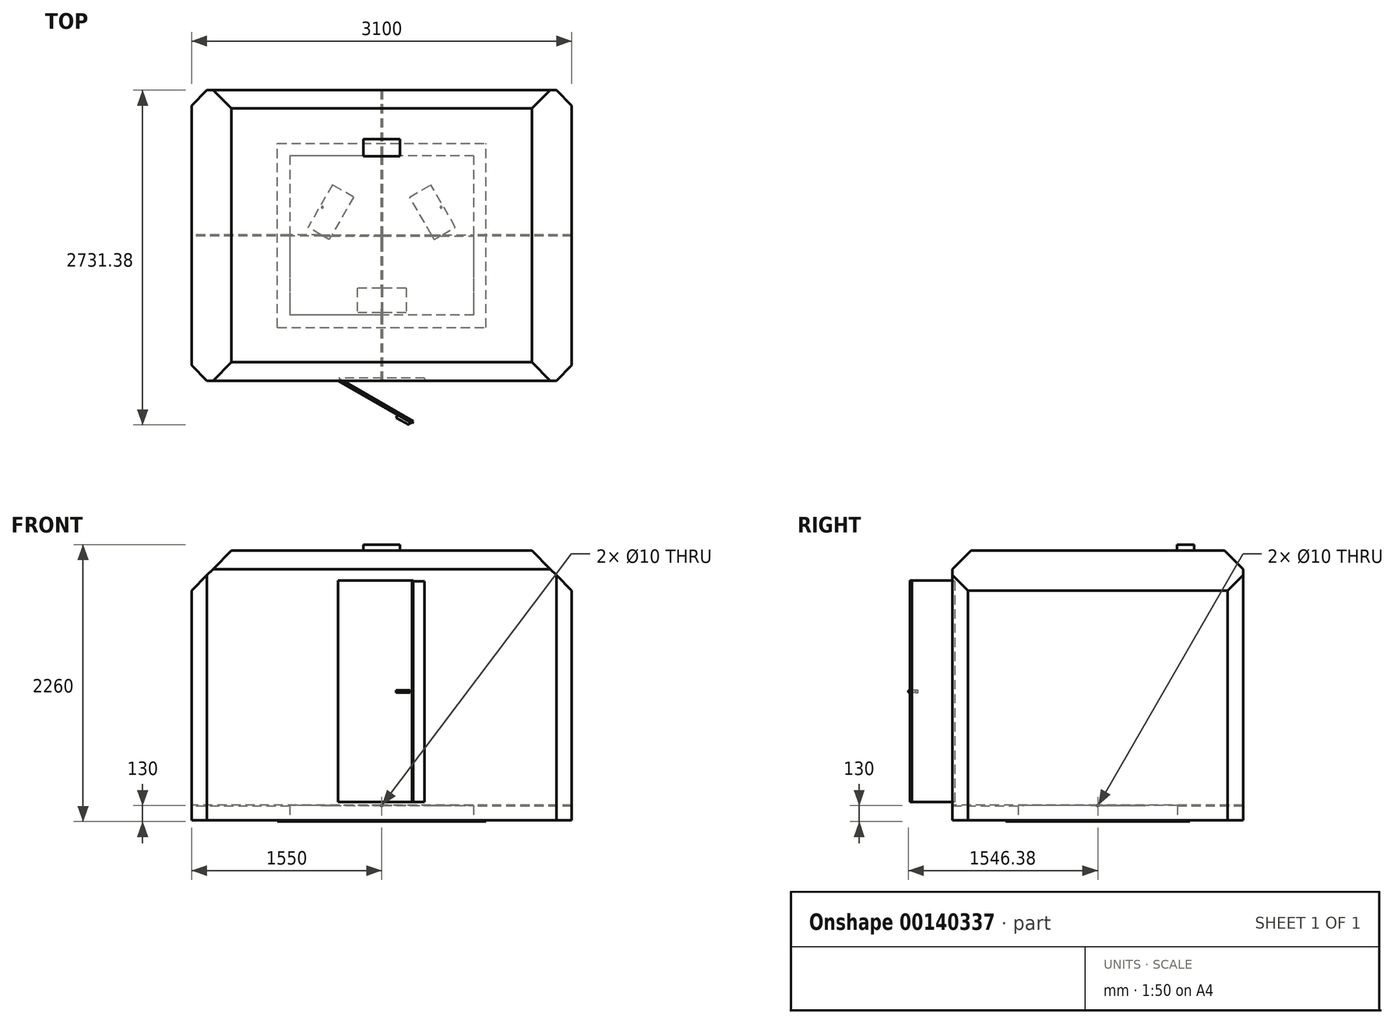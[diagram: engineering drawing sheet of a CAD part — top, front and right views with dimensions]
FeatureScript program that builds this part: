
annotation { "Feature Type Name" : "Feature", "Feature Type Description" : "" }
export const myFeature = defineFeature(function(context is Context, id is Id, definition is map)
    precondition{}
    {
        {
            var Q0;
            Q0=qCreatedBy(makeId("Front.planeOp"),FACE);
            var sketch = newSketch(context, id + "F0", { "sketchPlane" : qUnion([Q0])});
            skLineSegment(sketch, "E0.bottom", {"start": v(1550, -1100) * mm, "end": v(-1550, -1100) * mm});
            skLineSegment(sketch, "E0.top", {"start": v(1550, 1100) * mm, "end": v(-1550, 1100) * mm});
            skLineSegment(sketch, "E0.left", {"start": v(1550, -1100) * mm, "end": v(1550, 1100) * mm});
            skLineSegment(sketch, "E0.right", {"start": v(-1550, -1100) * mm, "end": v(-1550, 1100) * mm});
            skPoint(sketch, "E0.middle", {"position": v(0, 0) * mm});
            skSolve(sketch);
        }
        {
            var Q0;
            Q0 = qSketchRegion(id + "F0", true);
            extrude(context, id + "F1", {"entities" : qUnion([Q0]), "depth" : 2370 * mm});
        }
        {
            var Q0;
            Q0=makeQuery(id+"F1.opExtrude","SWEPT_EDGE",EDGE,{"disambiguationData":[OSD([sQuery(id+"F0.wireOp",EDGE,"E0.top"),sQuery(id+"F0.wireOp",EDGE,"E0.right")])]});
            chamfer(context, id + "F2", {"entities" : qUnion([Q0]), "width" : 325 * mm, "tangentPropagation" : true});
        }
        {
            var Q0;
            Q0=makeQuery(id+"F1.opExtrude","SWEPT_EDGE",EDGE,{"disambiguationData":[OSD([sQuery(id+"F0.wireOp",EDGE,"E0.top"),sQuery(id+"F0.wireOp",EDGE,"E0.left")])]});
            chamfer(context, id + "F3", {"entities" : qUnion([Q0]), "width" : 325 * mm, "tangentPropagation" : true});
        }
        {
            var Q0;
            Q0=makeQuery(id+"F1.opExtrude","CAP_EDGE",EDGE,{"disambiguationData":[OSD([sQuery(id+"F0.wireOp",EDGE,"E0.left")])],"isStart":false});
            chamfer(context, id + "F4", {"entities" : qUnion([Q0]), "width" : 125 * mm, "tangentPropagation" : true});
        }
        {
            var Q0;
            Q0=makeQuery(id+"F1.opExtrude","CAP_EDGE",EDGE,{"disambiguationData":[OSD([sQuery(id+"F0.wireOp",EDGE,"E0.right")])],"isStart":false});
            chamfer(context, id + "F5", {"entities" : qUnion([Q0]), "width" : 125 * mm, "tangentPropagation" : true});
        }
        {
            var Q0;
            Q0=makeQuery(id+"F1.opExtrude","CAP_EDGE",EDGE,{"disambiguationData":[OSD([sQuery(id+"F0.wireOp",EDGE,"E0.right")])],"isStart":true});
            chamfer(context, id + "F6", {"entities" : qUnion([Q0]), "width" : 125 * mm, "tangentPropagation" : true});
        }
        {
            var Q0;
            Q0=makeQuery(id+"F1.opExtrude","CAP_EDGE",EDGE,{"disambiguationData":[OSD([sQuery(id+"F0.wireOp",EDGE,"E0.left")])],"isStart":true});
            chamfer(context, id + "F7", {"entities" : qUnion([Q0]), "width" : 125 * mm, "tangentPropagation" : true});
        }
        {
            var Q0;
            Q0=makeQuery(id+"F1.opExtrude","SWEPT_FACE",FACE,{"disambiguationData":[OSD([sQuery(id+"F0.wireOp",EDGE,"E0.bottom")])]});
            var sketch = newSketch(context, id + "F8", { "sketchPlane" : qUnion([Q0])});
            skLineSegment(sketch, "E1", {"start": v(0, 0) * mm, "end": v(0, 2370) * mm, "construction": true});
            skLineSegment(sketch, "E2", {"start": v(-1550, 1185) * mm, "end": v(1550, 1185) * mm, "construction": true});
            skLineSegment(sketch, "E3.bottom", {"start": v(750, 535) * mm, "end": v(-750, 535) * mm});
            skLineSegment(sketch, "E3.top", {"start": v(750, 1835) * mm, "end": v(-750, 1835) * mm});
            skLineSegment(sketch, "E3.left", {"start": v(750, 535) * mm, "end": v(750, 1835) * mm});
            skLineSegment(sketch, "E3.right", {"start": v(-750, 535) * mm, "end": v(-750, 1835) * mm});
            skPoint(sketch, "E3.middle", {"position": v(0, 1185) * mm});
            skSolve(sketch);
        }
        {
            var Q0;
            Q0 = qSketchRegion(id + "F8", true);
            extrude(context, id + "F9", {"entities" : qUnion([Q0]), "operationType" : NewBodyOperationType.REMOVE, "oppositeDirection" : true, "depth" : 120 * mm});
        }
        {
            var Q0;
            Q0=makeQuery(id+"F9.boolean.opBoolean","COPY",FACE,{"derivedFrom":makeQuery(id+"F9.opExtrude","CAP_FACE",FACE,{"disambiguationData":[OSD([sQuery(id+"F8.wireOp",EDGE,"E3.bottom"),sQuery(id+"F8.wireOp",EDGE,"E3.top"),sQuery(id+"F8.wireOp",EDGE,"E3.left"),sQuery(id+"F8.wireOp",EDGE,"E3.right")])],"isStart":false})});
            var sketch = newSketch(context, id + "F10", { "sketchPlane" : qUnion([Q0])});
            skLineSegment(sketch, "E4", {"start": v(0, 1835) * mm, "end": v(0, 1235) * mm, "construction": true});
            skLineSegment(sketch, "E5.bottom", {"start": v(200, 1614) * mm, "end": v(-200, 1614) * mm});
            skLineSegment(sketch, "E5.top", {"start": v(200, 1814) * mm, "end": v(-200, 1814) * mm});
            skLineSegment(sketch, "E5.left", {"start": v(200, 1614) * mm, "end": v(200, 1814) * mm});
            skLineSegment(sketch, "E5.right", {"start": v(-200, 1614) * mm, "end": v(-200, 1814) * mm});
            skPoint(sketch, "E5.middle", {"position": v(0, 1714) * mm});
            skLineSegment(sketch, "E6", {"start": v(0, 1235) * mm, "end": v(-409.07, 998.82) * mm, "construction": true});
            skLineSegment(sketch, "E7", {"start": v(0, 1235) * mm, "end": v(395.82, 1006.47) * mm, "construction": true});
            skCircle(sketch, "E8", {"center": v(0, 1235) * mm, "radius": 559 * mm, "construction": true});
            skCircle(sketch, "E9", {"center": v(0, 1794) * mm, "radius": 7.5 * mm});
            skCircle(sketch, "E10.MirrorC", {"center": v(484.1, 955.5) * mm, "radius": 7.5 * mm});
            skCircle(sketch, "E11.MirrorC", {"center": v(-484.1, 955.5) * mm, "radius": 7.5 * mm});
            skLineSegment(sketch, "E12", {"start": v(750, 1185) * mm, "end": v(-750, 1185) * mm, "construction": true});
            skLineSegment(sketch, "E13.MirrorCS", {"start": v(428.22, 1218.7) * mm, "end": v(228.22, 872.3) * mm});
            skLineSegment(sketch, "E14.MirrorCS", {"start": v(228.22, 872.3) * mm, "end": v(401.43, 772.3) * mm});
            skLineSegment(sketch, "E15.MirrorCS", {"start": v(601.43, 1118.7) * mm, "end": v(401.43, 772.3) * mm});
            skLineSegment(sketch, "E16.MirrorCS", {"start": v(428.22, 1218.7) * mm, "end": v(601.43, 1118.7) * mm});
            skLineSegment(sketch, "E17.MirrorCS", {"start": v(-428.22, 1218.7) * mm, "end": v(-601.43, 1118.7) * mm});
            skLineSegment(sketch, "E18.MirrorCS", {"start": v(-401.43, 772.3) * mm, "end": v(-601.43, 1118.7) * mm});
            skLineSegment(sketch, "E19.MirrorCS", {"start": v(-228.22, 872.3) * mm, "end": v(-401.43, 772.3) * mm});
            skLineSegment(sketch, "E20.MirrorCS", {"start": v(-228.22, 872.3) * mm, "end": v(-428.22, 1218.7) * mm});
            skCircle(sketch, "E21", {"center": v(0, 1235) * mm, "radius": 7.5 * mm});
            skSolve(sketch);
        }
        {
            var Q0;
            Q0 = qSketchRegion(id + "F10", true);
            extrude(context, id + "F11", {"entities" : qUnion([Q0]), "operationType" : NewBodyOperationType.REMOVE, "oppositeDirection" : true, "depth" : 1 * mm});
        }
        {
            var Q0;
            Q0=makeQuery(id+"F9.boolean.opBoolean","COPY",FACE,{"derivedFrom":makeQuery(id+"F9.opExtrude","SWEPT_FACE",FACE,{"disambiguationData":[OSD([sQuery(id+"F8.wireOp",EDGE,"E3.right")])]})});
            var sketch = newSketch(context, id + "F12", { "sketchPlane" : qUnion([Q0])});
            skCircle(sketch, "E22", {"center": v(-1185, -980) * mm, "radius": 5 * mm});
            skSolve(sketch);
        }
        {
            var Q0;
            Q0 = qSketchRegion(id + "F12", true);
            extrude(context, id + "F13", {"entities" : qUnion([Q0]), "operationType" : NewBodyOperationType.REMOVE, "depth" : 1 * mm});
        }
        {
            var Q0;
            Q0 = qSketchRegion(id + "F12", true);
            extrude(context, id + "F14", {"entities" : qUnion([Q0]), "operationType" : NewBodyOperationType.REMOVE, "endBound" : BoundingType.THROUGH_ALL, "oppositeDirection" : true, "depth" : 25 * mm, "hasSecondDirection" : true, "secondDirectionBound" : SecondDirectionBoundingType.THROUGH_ALL, "secondDirectionOppositeDirection" : false, "secondDirectionDepth" : 25 * mm});
        }
        {
            var Q0;
            Q0=makeQuery(id+"F9.boolean.opBoolean","COPY",FACE,{"derivedFrom":makeQuery(id+"F9.opExtrude","SWEPT_FACE",FACE,{"disambiguationData":[OSD([sQuery(id+"F8.wireOp",EDGE,"E3.bottom")])]})});
            var sketch = newSketch(context, id + "F15", { "sketchPlane" : qUnion([Q0])});
            skLineSegment(sketch, "E23", {"start": v(0, -1100) * mm, "end": v(0, -980) * mm, "construction": true});
            skCircle(sketch, "E24", {"center": v(0, -980) * mm, "radius": 5 * mm});
            skSolve(sketch);
        }
        {
            var Q0;
            Q0 = qSketchRegion(id + "F15", true);
            extrude(context, id + "F16", {"entities" : qUnion([Q0]), "operationType" : NewBodyOperationType.REMOVE, "endBound" : BoundingType.THROUGH_ALL, "oppositeDirection" : true, "depth" : 25 * mm, "hasSecondDirection" : true, "secondDirectionBound" : SecondDirectionBoundingType.THROUGH_ALL, "secondDirectionOppositeDirection" : false, "secondDirectionDepth" : 25 * mm});
        }
        {
            var Q0;
            Q0=makeQuery(id+"F1.opExtrude","CAP_EDGE",EDGE,{"disambiguationData":[OSD([sQuery(id+"F0.wireOp",EDGE,"E0.top")])],"isStart":true});
            chamfer(context, id + "F17", {"entities" : qUnion([Q0]), "width" : 150 * mm, "tangentPropagation" : true});
        }
        {
            var Q0;
            Q0=makeQuery(id+"F1.opExtrude","CAP_EDGE",EDGE,{"disambiguationData":[OSD([sQuery(id+"F0.wireOp",EDGE,"E0.top")])],"isStart":false});
            chamfer(context, id + "F18", {"entities" : qUnion([Q0]), "width" : 150 * mm, "tangentPropagation" : true});
        }
        {
            var Q0;
            Q0=makeQuery(id+"F1.opExtrude","SWEPT_FACE",FACE,{"disambiguationData":[OSD([sQuery(id+"F0.wireOp",EDGE,"E0.bottom")])]});
            var sketch = newSketch(context, id + "F19", { "sketchPlane" : qUnion([Q0])});
            skLineSegment(sketch, "E25.bottom", {"start": v(-850, 1935) * mm, "end": v(850, 1935) * mm});
            skLineSegment(sketch, "E25.top", {"start": v(-850, 435) * mm, "end": v(850, 435) * mm});
            skLineSegment(sketch, "E25.left", {"start": v(-850, 1935) * mm, "end": v(-850, 435) * mm});
            skLineSegment(sketch, "E25.right", {"start": v(850, 1935) * mm, "end": v(850, 435) * mm});
            skLineSegment(sketch, "E26.bottom", {"start": v(-750, 535) * mm, "end": v(750, 535) * mm});
            skLineSegment(sketch, "E26.top", {"start": v(-750, 1835) * mm, "end": v(750, 1835) * mm});
            skLineSegment(sketch, "E26.left", {"start": v(-750, 535) * mm, "end": v(-750, 1835) * mm});
            skLineSegment(sketch, "E26.right", {"start": v(750, 535) * mm, "end": v(750, 1835) * mm});
            skSolve(sketch);
        }
        {
            var Q0;
            Q0 = qSketchRegion(id + "F19", true);
            extrude(context, id + "F20", {"entities" : qUnion([Q0]), "operationType" : NewBodyOperationType.ADD, "depth" : 10 * mm});
        }
        {
            var Q0;
            Q0=makeQuery(id+"F1.opExtrude","CAP_FACE",FACE,{"disambiguationData":[OSD([sQuery(id+"F0.wireOp",EDGE,"E0.bottom"),sQuery(id+"F0.wireOp",EDGE,"E0.top"),sQuery(id+"F0.wireOp",EDGE,"E0.left"),sQuery(id+"F0.wireOp",EDGE,"E0.right")])],"isStart":false});
            var sketch = newSketch(context, id + "F21", { "sketchPlane" : qUnion([Q0])});
            skLineSegment(sketch, "E27", {"start": v(0, 950) * mm, "end": v(0, -367.55) * mm, "construction": true});
            skPoint(sketch, "E28.middle", {"position": v(0, -75) * mm});
            skPoint(sketch, "E29.middle", {"position": v(0, -1025) * mm});
            skLineSegment(sketch, "E30.bottom", {"start": v(350, -950) * mm, "end": v(-350, -950) * mm});
            skLineSegment(sketch, "E30.top", {"start": v(350, 850) * mm, "end": v(-350, 850) * mm});
            skLineSegment(sketch, "E30.left", {"start": v(350, -950) * mm, "end": v(350, 850) * mm});
            skLineSegment(sketch, "E30.right", {"start": v(-350, -950) * mm, "end": v(-350, 850) * mm});
            skPoint(sketch, "E30.middle", {"position": v(0, -50) * mm});
            skSolve(sketch);
        }
        {
            var Q0;
            Q0 = qSketchRegion(id + "F21", true);
            extrude(context, id + "F22", {"entities" : qUnion([Q0]), "operationType" : NewBodyOperationType.REMOVE, "oppositeDirection" : true, "depth" : 20 * mm});
        }
        {
            var Q0;
            Q0=makeQuery(id+"F1.opExtrude","SWEPT_FACE",FACE,{"disambiguationData":[OSD([sQuery(id+"F0.wireOp",EDGE,"E0.top")])]});
            var sketch = newSketch(context, id + "F23", { "sketchPlane" : qUnion([Q0])});
            skLineSegment(sketch, "E31", {"start": v(0, -150) * mm, "end": v(0, -1860.94) * mm, "construction": true});
            skPoint(sketch, "E31.endSnap0", {"position": v(0, -150) * mm});
            skLineSegment(sketch, "E32.bottom", {"start": v(150, -540) * mm, "end": v(-150, -540) * mm});
            skLineSegment(sketch, "E32.top", {"start": v(150, -400) * mm, "end": v(-150, -400) * mm});
            skLineSegment(sketch, "E32.left", {"start": v(150, -540) * mm, "end": v(150, -400) * mm});
            skLineSegment(sketch, "E32.right", {"start": v(-150, -540) * mm, "end": v(-150, -400) * mm});
            skPoint(sketch, "E32.middle", {"position": v(0, -470) * mm});
            skSolve(sketch);
        }
        {
            var Q0;
            Q0 = qSketchRegion(id + "F23", true);
            extrude(context, id + "F24", {"entities" : qUnion([Q0]), "operationType" : NewBodyOperationType.ADD, "depth" : 50 * mm});
        }
        {
            var Q0;
            Q0=makeQuery(id+"F22.boolean.opBoolean","COPY",FACE,{"derivedFrom":makeQuery(id+"F22.opExtrude","SWEPT_FACE",FACE,{"disambiguationData":[OSD([sQuery(id+"F21.wireOp",EDGE,"E30.bottom")])]})});
            var sketch = newSketch(context, id + "F25", { "sketchPlane" : qUnion([Q0])});
            skLineSegment(sketch, "E33.bottom", {"start": v(-360, -2367.32) * mm, "end": v(246.22, -2717.32) * mm});
            skLineSegment(sketch, "E33.top", {"start": v(-350, -2350) * mm, "end": v(256.22, -2700) * mm});
            skLineSegment(sketch, "E33.left", {"start": v(-360, -2367.32) * mm, "end": v(-350, -2350) * mm});
            skLineSegment(sketch, "E33.right", {"start": v(246.22, -2717.32) * mm, "end": v(256.22, -2700) * mm});
            skSolve(sketch);
        }
        {
            var Q0;
            Q0 = qSketchRegion(id + "F25", true);
            extrude(context, id + "F26", {"entities" : qUnion([Q0]), "operationType" : NewBodyOperationType.ADD, "depth" : 1805 * mm});
        }
        {
            var Q0;
            Q0=makeQuery(id+"F26.opExtrude","SWEPT_FACE",FACE,{"disambiguationData":[OSD([sQuery(id+"F25.wireOp",EDGE,"E33.bottom")])]});
            var sketch = newSketch(context, id + "F27", { "sketchPlane" : qUnion([Q0])});
            skLineSegment(sketch, "E34.bottom", {"start": v(1436.7, -57.5) * mm, "end": v(1556.7, -57.5) * mm});
            skLineSegment(sketch, "E34.top", {"start": v(1436.7, -37.5) * mm, "end": v(1556.7, -37.5) * mm});
            skLineSegment(sketch, "E34.left", {"start": v(1436.7, -57.5) * mm, "end": v(1436.7, -37.5) * mm});
            skLineSegment(sketch, "E34.right", {"start": v(1556.7, -57.5) * mm, "end": v(1556.7, -37.5) * mm});
            skPoint(sketch, "E34.middle", {"position": v(1496.7, -47.5) * mm});
            skPoint(sketch, "E34.middle.positionSnap0", {"position": v(1571.9, -47.5) * mm});
            skPoint(sketch, "E34.centerSnap0", {"position": v(1571.9, -47.5) * mm});
            skSolve(sketch);
        }
        {
            var Q0;
            Q0 = qSketchRegion(id + "F27", true);
            extrude(context, id + "F28", {"entities" : qUnion([Q0]), "operationType" : NewBodyOperationType.ADD, "depth" : 25 * mm});
        }
    });
